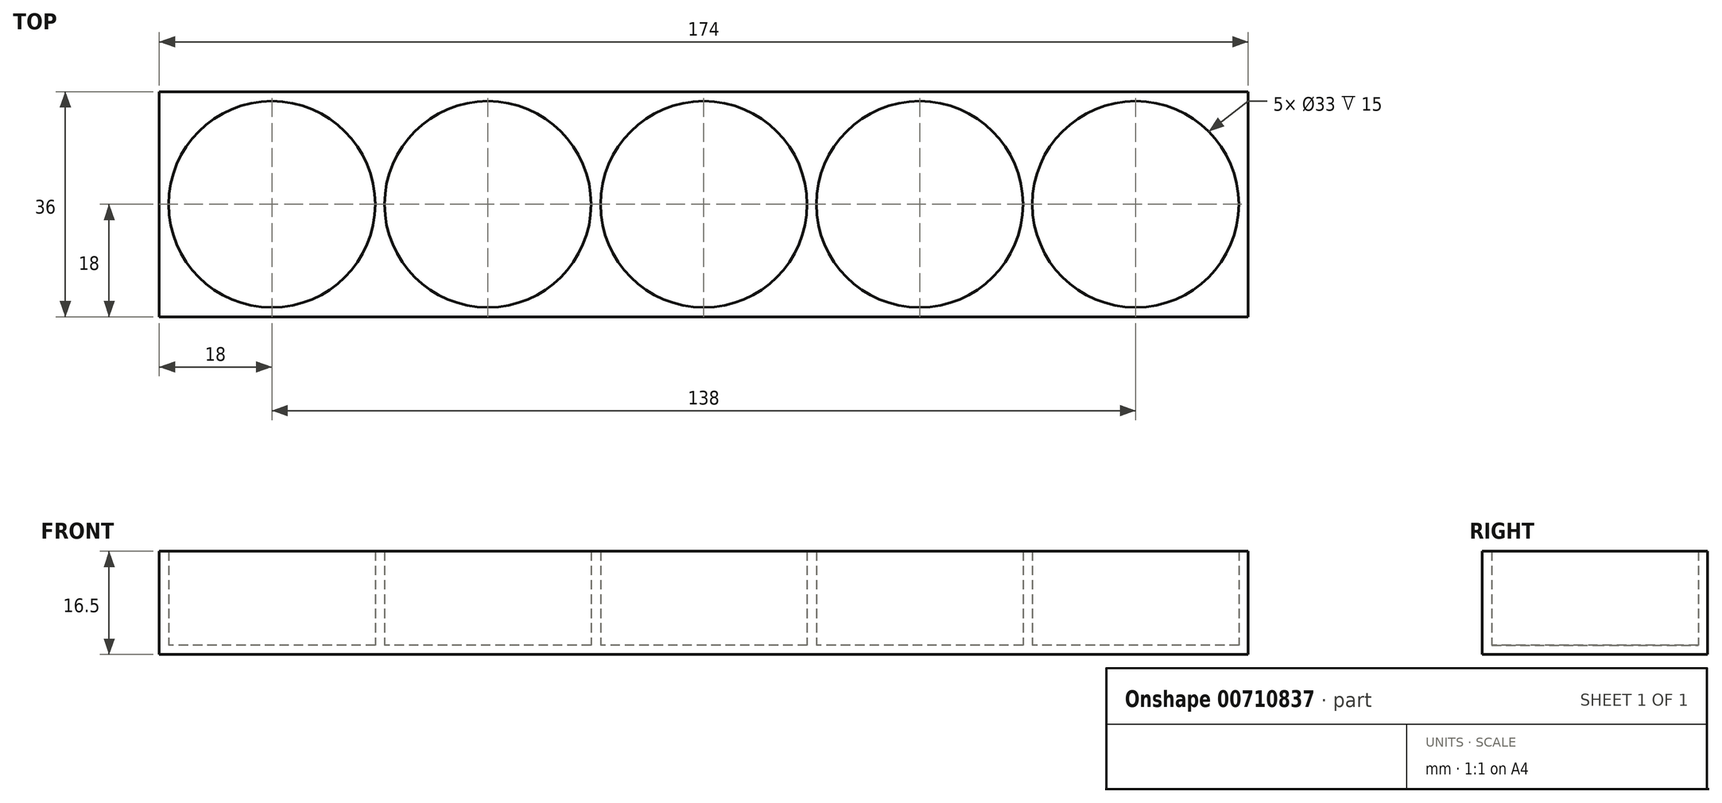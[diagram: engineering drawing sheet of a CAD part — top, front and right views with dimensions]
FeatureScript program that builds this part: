
annotation { "Feature Type Name" : "Feature", "Feature Type Description" : "" }
export const myFeature = defineFeature(function(context is Context, id is Id, definition is map)
    precondition{}
    {
        {
            var Q0;
            Q0=qCreatedBy(makeId("Top.planeOp"),FACE);
            var sketch = newSketch(context, id + "F0", { "sketchPlane" : qUnion([Q0])});
            skLineSegment(sketch, "E0.bottom", {"start": v(-67.08, 18) * mm, "end": v(106.92, 18) * mm});
            skLineSegment(sketch, "E0.top", {"start": v(-67.08, -18) * mm, "end": v(106.92, -18) * mm});
            skLineSegment(sketch, "E0.left", {"start": v(-67.08, 18) * mm, "end": v(-67.08, -18) * mm});
            skLineSegment(sketch, "E0.right", {"start": v(106.92, 18) * mm, "end": v(106.92, -18) * mm});
            skCircle(sketch, "E1", {"center": v(-49.08, 0) * mm, "radius": 16.5 * mm});
            skCircle(sketch, "E2.1.0.0", {"center": v(-14.58, 0) * mm, "radius": 16.5 * mm});
            skCircle(sketch, "E2.2.0.0", {"center": v(19.92, 0) * mm, "radius": 16.5 * mm});
            skCircle(sketch, "E2.3.0.0", {"center": v(54.42, 0) * mm, "radius": 16.5 * mm});
            skCircle(sketch, "E2.4.0.0", {"center": v(88.92, 0) * mm, "radius": 16.5 * mm});
            skLineSegment(sketch, "E2.direction1", {"start": v(-49.08, 0) * mm, "end": v(-14.58, 0) * mm, "construction": true});
            skSolve(sketch);
        }
        {
            var Q0;
            Q0=makeQuery(id+"F0.imprint","IMPRINT",FACE,{"disambiguationData":[TD([[makeQuery(id+"F0.imprint","IMPRINT",EDGE,{"derivedFrom":sQuery(id+"F0.wireOp",EDGE,"E0.bottom")}),-1.0]])]});
            extrude(context, id + "F1", {"entities" : qUnion([Q0]), "depth" : 15 * mm, "offsetDistance" : 25 * mm});
        }
        {
            var Q0;
            Q0=makeQuery(id+"F1.opExtrude","CAP_FACE",FACE,{"disambiguationData":[OSD([sQuery(id+"F0.wireOp",EDGE,"E0.bottom"),sQuery(id+"F0.wireOp",EDGE,"E0.top"),sQuery(id+"F0.wireOp",EDGE,"E0.left"),sQuery(id+"F0.wireOp",EDGE,"E0.right"),sQuery(id+"F0.wireOp",EDGE,"E1"),sQuery(id+"F0.wireOp",EDGE,"E2.1.0.0"),sQuery(id+"F0.wireOp",EDGE,"E2.2.0.0"),sQuery(id+"F0.wireOp",EDGE,"E2.3.0.0"),sQuery(id+"F0.wireOp",EDGE,"E2.4.0.0")])],"isStart":true});
            var sketch = newSketch(context, id + "F2", { "sketchPlane" : qUnion([Q0])});
            skLineSegment(sketch, "E3.bottom", {"start": v(-67.08, 18) * mm, "end": v(106.92, 18) * mm});
            skLineSegment(sketch, "E3.top", {"start": v(-67.08, -18) * mm, "end": v(106.92, -18) * mm});
            skLineSegment(sketch, "E3.left", {"start": v(-67.08, 18) * mm, "end": v(-67.08, -18) * mm});
            skLineSegment(sketch, "E3.right", {"start": v(106.92, 18) * mm, "end": v(106.92, -18) * mm});
            skSolve(sketch);
        }
        {
            var Q0;
            Q0 = qSketchRegion(id + "F2", true);
            extrude(context, id + "F3", {"entities" : qUnion([Q0]), "operationType" : NewBodyOperationType.ADD, "depth" : 1.5 * mm, "offsetDistance" : 25 * mm});
        }
    });
